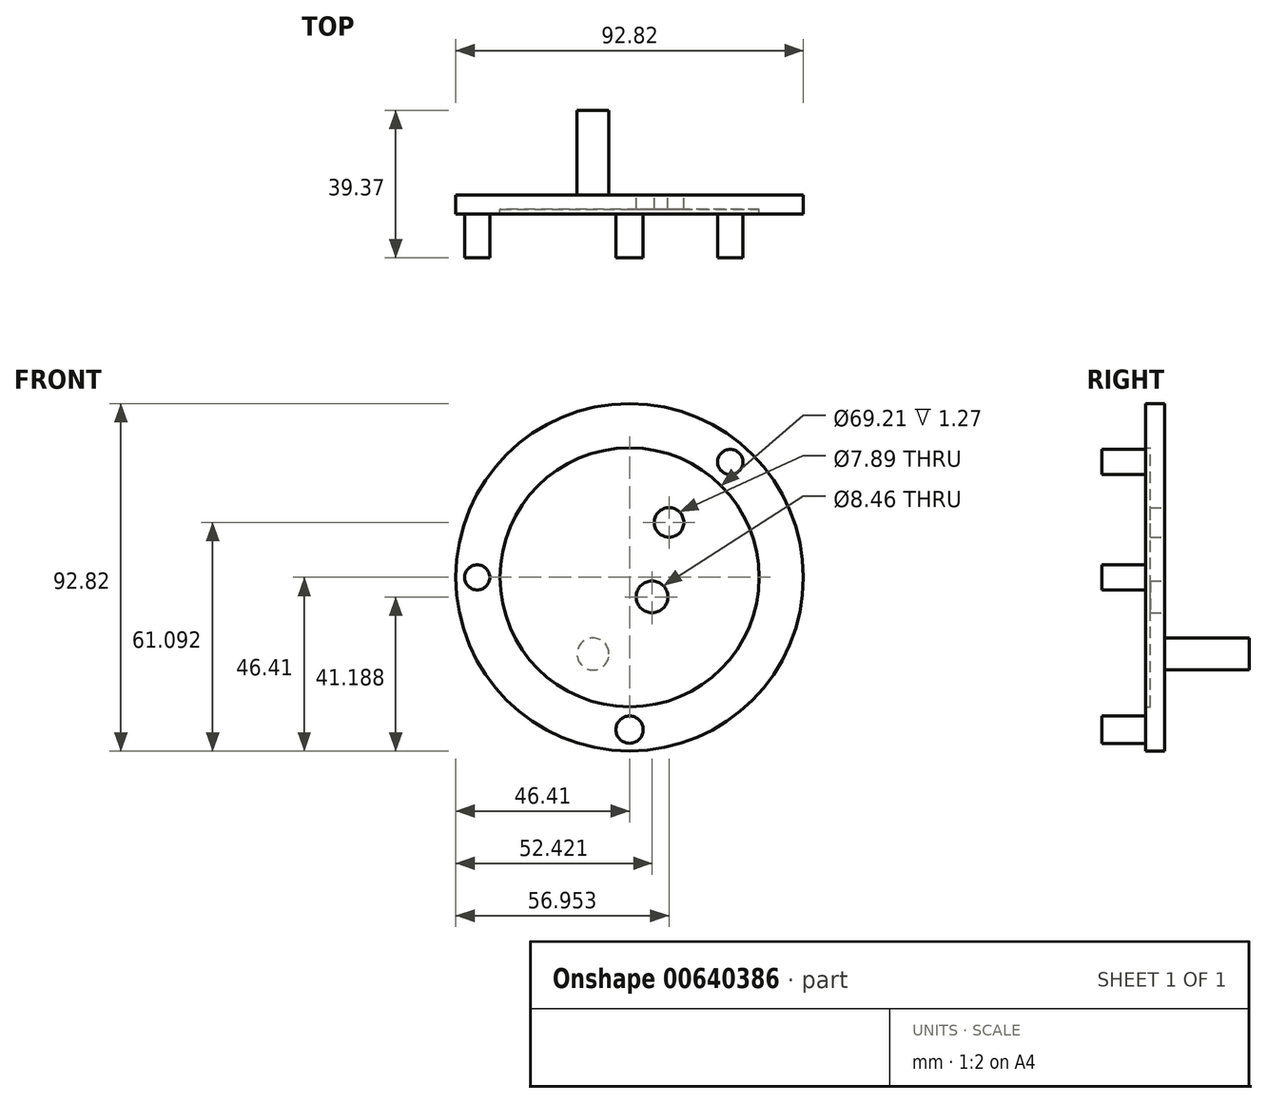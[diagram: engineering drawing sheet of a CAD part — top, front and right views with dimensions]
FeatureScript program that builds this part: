
annotation { "Feature Type Name" : "Feature", "Feature Type Description" : "" }
export const myFeature = defineFeature(function(context is Context, id is Id, definition is map)
    precondition{}
    {
        {
            var Q0;
            Q0=qCreatedBy(makeId("Front.planeOp"),FACE);
            var sketch = newSketch(context, id + "F0", { "sketchPlane" : qUnion([Q0])});
            skCircle(sketch, "E0", {"center": v(0, 0) * mm, "radius": 46.41 * mm});
            skCircle(sketch, "E1", {"center": v(0, 0) * mm, "radius": 34.6 * mm});
            skCircle(sketch, "E2", {"center": v(10.54, 14.68) * mm, "radius": 3.95 * mm});
            skCircle(sketch, "E3", {"center": v(6.01, -5.22) * mm, "radius": 4.23 * mm});
            skCircle(sketch, "E4", {"center": v(-40.7, 0) * mm, "radius": 3.35 * mm});
            skCircle(sketch, "E5", {"center": v(0, -40.7) * mm, "radius": 3.65 * mm});
            skCircle(sketch, "E6", {"center": v(26.9, 30.84) * mm, "radius": 3.37 * mm});
            skSolve(sketch);
        }
        {
            var Q0;
            Q0=makeQuery(id+"F0.imprint","IMPRINT",FACE,{"disambiguationData":[TD([[makeQuery(id+"F0.imprint","IMPRINT",EDGE,{"derivedFrom":sQuery(id+"F0.wireOp",EDGE,"E0")}),1.0]])]});
            extrude(context, id + "F1", {"entities" : qUnion([Q0]), "depth" : 5.08 * mm, "offsetDistance" : 25.4 * mm});
        }
        {
            var Q0;
            Q0=makeQuery(id+"F0.imprint","IMPRINT",FACE,{"disambiguationData":[TD([[makeQuery(id+"F0.imprint","IMPRINT",EDGE,{"derivedFrom":sQuery(id+"F0.wireOp",EDGE,"E1")}),1.0]])]});
            extrude(context, id + "F2", {"entities" : qUnion([Q0]), "operationType" : NewBodyOperationType.ADD, "depth" : 3.8 * mm, "offsetDistance" : 25.4 * mm});
        }
        {
            var Q0;
            Q0=makeQuery(id+"F0.imprint","IMPRINT",FACE,{"disambiguationData":[TD([[makeQuery(id+"F0.imprint","IMPRINT",EDGE,{"derivedFrom":sQuery(id+"F0.wireOp",EDGE,"E4")}),1.0]])]});
            extrude(context, id + "F3", {"entities" : qUnion([Q0]), "operationType" : NewBodyOperationType.ADD, "depth" : 16.76 * mm, "offsetDistance" : 25.4 * mm});
        }
        {
            var Q0;
            Q0=makeQuery(id+"F0.imprint","IMPRINT",FACE,{"disambiguationData":[TD([[makeQuery(id+"F0.imprint","IMPRINT",EDGE,{"derivedFrom":sQuery(id+"F0.wireOp",EDGE,"E5")}),1.0]])]});
            var Q1;
            Q1=makeQuery(id+"F0.imprint","IMPRINT",FACE,{"disambiguationData":[TD([[makeQuery(id+"F0.imprint","IMPRINT",EDGE,{"derivedFrom":sQuery(id+"F0.wireOp",EDGE,"E6")}),1.0]])]});
            extrude(context, id + "F4", {"entities" : qUnion([Q0, Q1]), "operationType" : NewBodyOperationType.ADD, "depth" : 16.76 * mm, "offsetDistance" : 25.4 * mm});
        }
        {
            var Q0;
            Q0=qCreatedBy(makeId("Front.planeOp"),FACE);
            var sketch = newSketch(context, id + "F5", { "sketchPlane" : qUnion([Q0])});
            skCircle(sketch, "E7", {"center": v(-9.77, -20.47) * mm, "radius": 4.26 * mm});
            skSolve(sketch);
        }
        {
            var Q0;
            Q0=makeQuery(id+"F5.imprint","IMPRINT",FACE,{"disambiguationData":[TD([[makeQuery(id+"F5.imprint","IMPRINT",EDGE,{"derivedFrom":sQuery(id+"F5.wireOp",EDGE,"E7")}),1.0]])]});
            extrude(context, id + "F6", {"entities" : qUnion([Q0]), "operationType" : NewBodyOperationType.ADD, "oppositeDirection" : true, "depth" : 22.6 * mm, "offsetDistance" : 25.4 * mm});
        }
    });
